# Revit family: 0053938
name_source: partatom
category: Lighting Fixtures
revit_build: Autodesk Revit 2017 (Build: 20190507_1515(x64)
units: mm (PartAtom-declared; Revit-internal decimal feet)

## family parameters
Cut with Voids When Loaded = No
Host = Face
Light Source = Yes
OmniClass Number = 23.80.70.00
OmniClass Title = Lighting
Part Type = Normal
Room Calculation Point = No
Round Connector Dimension = Use Diameter
Shared = No

## types (17) — shared parameters
Assembly Code = D5020200
AssetType = Fixed
CHAMF_2_SYL = 1 mm  [stored 0.00328084 ft]
CHAMF_SYL = 1 mm  [stored 0.00328084 ft]
CLIP_CUTOUT_SYL = 19 mm  [stored 0.062336 ft]
CLIP_HOLE_HE_SYL = 9 mm
CLIP_HOLE_SYL = 3 mm  [stored 0.00984252 ft]
CLIP_SYL = 10 mm  [stored 0.0328084 ft]
ClassificationName = Uniclass2015
ClassificationValue = EF_70_80
Color Filter = 16777215
Default Elevation = 1219 mm
Dimming Lamp Color Temperature Shift = <None>
DocumentationLiterature = http://www.sylvania-lighting.com
ElectricShockClassification = Class II
Emit Shape Visible in Rendering = No
Emit from Circle Diameter = 610 mm
IfcExportAs = IfcLightFixtureType
IfcExportType = IfcLightFixtureType
ImpactProtectionIndex = IK06
IngressProtection = IP44/20
Keynote = 16500
LUM_HEIGHT_SYL = 14 mm  [stored 0.0459318 ft]
Lamp = LED
LampColourRenderingIndex = 80
LampsType = LED
Manufacturer = Feilo Sylvania
ManufacturerName = Feilo Sylvania
Material_1_SYL = <By Category>
Material_2_SYL = <By Category>
Material_3_SYL = <By Category>
Material_4_SYL = <By Category>
Tilt Angle = -90.00°
Type Image = <None>
URL = http://www.sylvania-lighting.com
Voltage = 0 V
zero-valued in all types: Cost

## per-type parameters (varying)
- 0053988 SYLFLAT 105 IP44 550LM 830 DIM: Apparent Load=7 VA; CLIP_DIST_SYL=75 mm  [stored 0.246063 ft]; CLIP_D_SYL=75 mm  [stored 0.246063 ft]; Description=Sylflat DIM is an integrated LED recessed downlight with separated phase dimmable driver; 7W; 550Lm; 79Lm/W; 3000K; IP44 rated from the front; 50,000hrs (L70B50).; LampColourTemperature=3000 K; LampMacAdamStep=3; LampNominalLuminous=550 lm; LuminousEfficacy=78.57 lm/W; Model=Sylflat 105 IP44 550lm 830 DIM; ModelNumber=53988; ModelReference=Sylflat 105 IP44 550lm 830 DIM; Name=Sylflat 105 IP44 550lm 830 DIM; NominalDepth=0 mm  [stored 0 ft]; NominalHeight=0 mm  [stored 0 ft]; NominalLength=0 mm  [stored 0 ft]; Photometric Web File=0053988.ies; PowerConsumption=7 W; PowerFactor=0; R1_SYL=86 mm  [stored 0.282152 ft]; R2_SYL=78 mm; R_DIFF_SYL=64 mm; SIZE_155_SYL=1; SIZE_203_SYL=0; TypeName=Sylflat 105 IP44 550lm 830 DIM; Weight=3.555 kg
- 0053957 SYLFLAT 205 IP44 2250LM 840 DIM: Apparent Load=24 VA; CLIP_DIST_SYL=99 mm  [stored 0.324803 ft]; CLIP_D_SYL=99 mm  [stored 0.324803 ft]; Description=Sylflat DIM is an integrated LED recessed downlight with separated phase dimmable driver; 24W; 2250Lm; 103Lm/W; 4000K; IP44 rated from the front; 50,000hrs (L70B50).; LampColourTemperature=4000 K; LampMacAdamStep=3; LampNominalLuminous=2250 lm; LuminousEfficacy=103 lm/W; Model=Sylflat 205 IP44 2250lm 840 DIM; ModelNumber=53957; ModelReference=Sylflat 205 IP44 2250lm 840 DIM; Name=Sylflat 205 IP44 2250lm 840 DIM; NominalDepth=226 mm  [stored 0.74147 ft]; NominalHeight=21 mm  [stored 0.0688976 ft]; NominalLength=226 mm  [stored 0.74147 ft]; Photometric Web File=0053957.ies; PowerConsumption=24 W; PowerFactor=0.9; R1_SYL=113 mm  [stored 0.370735 ft]; R2_SYL=102 mm; R_DIFF_SYL=87 mm; SIZE_155_SYL=0; SIZE_203_SYL=1; TypeName=Sylflat 205 IP44 2250lm 840 DIM; Weight=4.57 kg
- 0053956 SYLFLAT 205 IP44 2200LM 830 DIM: Apparent Load=24 VA; CLIP_DIST_SYL=99 mm  [stored 0.324803 ft]; CLIP_D_SYL=99 mm  [stored 0.324803 ft]; Description=Sylflat DIM is an integrated LED recessed downlight with separated phase dimmable driver; 24W; 2200Lm; 100Lm/W; 3000K; IP44 rated from the front; 50,000hrs (L70B50).; LampColourTemperature=3000 K; LampMacAdamStep=3; LampNominalLuminous=2200 lm; LuminousEfficacy=100 lm/W; Model=Sylflat 205 IP44 2200lm 830 DIM; ModelNumber=53956; ModelReference=Sylflat 205 IP44 2200lm 830 DIM; Name=Sylflat 205 IP44 2200lm 830 DIM; NominalDepth=226 mm  [stored 0.74147 ft]; NominalHeight=21 mm  [stored 0.0688976 ft]; NominalLength=226 mm  [stored 0.74147 ft]; Photometric Web File=0053956.ies; PowerConsumption=24 W; PowerFactor=0.9; R1_SYL=113 mm  [stored 0.370735 ft]; R2_SYL=102 mm; R_DIFF_SYL=87 mm; SIZE_155_SYL=0; SIZE_203_SYL=1; TypeName=Sylflat 205 IP44 2200lm 830 DIM; Weight=4.57 kg
- 0053955 SYLFLAT 205 IP44 1750LM 840 DIM: Apparent Load=17 VA; CLIP_DIST_SYL=99 mm  [stored 0.324803 ft]; CLIP_D_SYL=99 mm  [stored 0.324803 ft]; Description=Sylflat DIM is an integrated LED recessed downlight with separated phase dimmable driver; 17W; 1750Lm; 103Lm/W; 4000K; IP44 rated from the front; 50,000hrs (L70B50).; LampColourTemperature=4000 K; LampMacAdamStep=3; LampNominalLuminous=1750 lm; LuminousEfficacy=103 lm/W; Material=aluminium housing, other diffuser; Model=Sylflat 205 IP44 1750lm 840 DIM; ModelNumber=53955; ModelReference=Sylflat 205 IP44 1750lm 840 DIM; Name=Sylflat 205 IP44 1750lm 840 DIM; NominalDepth=226 mm  [stored 0.74147 ft]; NominalHeight=21 mm  [stored 0.0688976 ft]; NominalLength=226 mm  [stored 0.74147 ft]; Photometric Web File=0053955.ies; PowerConsumption=17 W; PowerFactor=0.9; R1_SYL=113 mm  [stored 0.370735 ft]; R2_SYL=102 mm; R_DIFF_SYL=87 mm; SIZE_155_SYL=0; SIZE_203_SYL=1; TypeName=Sylflat 205 IP44 1750lm 840 DIM; Weight=4.57 kg
- 0053954 SYLFLAT 205 IP44 1550LM 830 DIM: Apparent Load=17 VA; CLIP_DIST_SYL=99 mm  [stored 0.324803 ft]; CLIP_D_SYL=99 mm  [stored 0.324803 ft]; Description=Sylflat DIM is an integrated LED recessed downlight with separated phase dimmable driver; 17W; 1550Lm; 91Lm/W; 3000K; IP44 rated from the front; 50,000hrs (L70B50).; LampColourTemperature=3000 K; LampMacAdamStep=3; LampNominalLuminous=1550 lm; LuminousEfficacy=91 lm/W; Material=aluminium housing, other diffuser; Model=Sylflat 205 IP44 1550lm 830 DIM; ModelNumber=53954; ModelReference=Sylflat 205 IP44 1550lm 830 DIM; Name=Sylflat 205 IP44 1550lm 830 DIM; NominalDepth=226 mm  [stored 0.74147 ft]; NominalHeight=21 mm  [stored 0.0688976 ft]; NominalLength=226 mm  [stored 0.74147 ft]; Photometric Web File=0053954.ies; PowerConsumption=17 W; PowerFactor=0.9; R1_SYL=113 mm  [stored 0.370735 ft]; R2_SYL=102 mm; R_DIFF_SYL=87 mm; SIZE_155_SYL=0; SIZE_203_SYL=1; TypeName=Sylflat 205 IP44 1550lm 830 DIM; Weight=4.57 kg
- 0053953 SYLFLAT 155 IP44 1100LM 840 DIM: Apparent Load=12 VA; CLIP_DIST_SYL=75 mm  [stored 0.246063 ft]; CLIP_D_SYL=75 mm  [stored 0.246063 ft]; Description=Sylflat DIM is an integrated LED recessed downlight with separated phase dimmable driver; 12W; 1100Lm; 92Lm/W; 4000K; IP44 rated from the front; 50,000hrs (L70B50).; LampColourTemperature=4000 K; LampMacAdamStep=3; LampNominalLuminous=1100 lm; LuminousEfficacy=92 lm/W; Material=aluminium housing, other diffuser; Model=Sylflat 155 IP44 1100lm 840 DIM; ModelNumber=53953; ModelReference=Sylflat 155 IP44 1100lm 840 DIM; Name=Sylflat 155 IP44 1100lm 840 DIM; NominalDepth=172 mm  [stored 0.564304 ft]; NominalHeight=21 mm  [stored 0.0688976 ft]; NominalLength=172 mm  [stored 0.564304 ft]; Photometric Web File=0053953.ies; PowerConsumption=12 W; PowerFactor=0.9; R1_SYL=86 mm  [stored 0.282152 ft]; R2_SYL=78 mm; R_DIFF_SYL=64 mm; SIZE_155_SYL=1; SIZE_203_SYL=0; TypeName=Sylflat 155 IP44 1100lm 840 DIM; Weight=3.27 kg
- 0053952 SYLFLAT 155 IP44 1000LM 830 DIM: Apparent Load=12 VA; CLIP_DIST_SYL=75 mm  [stored 0.246063 ft]; CLIP_D_SYL=75 mm  [stored 0.246063 ft]; Description=Sylflat DIM is an integrated LED recessed downlight with separated phase dimmable driver; 12W; 1000Lm; 83Lm/W; 3000K; IP44 rated from the front; 50,000hrs (L70B50).; LampColourTemperature=3000 K; LampMacAdamStep=3; LampNominalLuminous=1000 lm; LuminousEfficacy=83 lm/W; Material=aluminium housing, other diffuser; Model=Sylflat 155 IP44 1000lm 830 DIM; ModelNumber=53952; ModelReference=Sylflat 155 IP44 1000lm 830 DIM; Name=Sylflat 155 IP44 1000lm 830 DIM; NominalDepth=172 mm  [stored 0.564304 ft]; NominalHeight=21 mm  [stored 0.0688976 ft]; NominalLength=172 mm  [stored 0.564304 ft]; Photometric Web File=0053952.ies; PowerConsumption=12 W; PowerFactor=0.9; R1_SYL=86 mm  [stored 0.282152 ft]; R2_SYL=78 mm; R_DIFF_SYL=64 mm; SIZE_155_SYL=1; SIZE_203_SYL=0; TypeName=Sylflat 155 IP44 1000lm 830 DIM; Weight=3.27 kg
- 0053951 ST E DOWNLIGHT FLT 205 IP44 2200 865 DIM: Apparent Load=24 VA; CLIP_DIST_SYL=99 mm  [stored 0.324803 ft]; CLIP_D_SYL=99 mm  [stored 0.324803 ft]; Description=START eco Downlight Flat IP44 DIM is an integrated LED recessed downlight with separated phase dimmable driver; 24W; 2200Lm; 92Lm/W; 6500K; IP44 rated from the front; 30,000hrs (L70B50).; LampColourTemperature=6500 K; LampMacAdamStep=5; LampNominalLuminous=2200 lm; LuminousEfficacy=92 lm/W; Model=START eco Downlight Flat 205 IP44 2200lm 865 DIM; ModelNumber=53951; ModelReference=START eco Downlight Flat 205 IP44 2200lm 865 DIM; Name=START eco Downlight Flat 205 IP44 2200lm 865 DIM; NominalDepth=226 mm  [stored 0.74147 ft]; NominalHeight=21 mm  [stored 0.0688976 ft]; NominalLength=226 mm  [stored 0.74147 ft]; Photometric Web File=0053951.ies; PowerConsumption=24 W; PowerFactor=0.9; R1_SYL=113 mm  [stored 0.370735 ft]; R2_SYL=102 mm; R_DIFF_SYL=87 mm; SIZE_155_SYL=0; SIZE_203_SYL=1; TypeName=START eco Downlight Flat 205 IP44 2200lm 865 DIM; Weight=4.57 kg
- 0053950 ST E DOWNLIGHT FLT 205 IP44 1700 865 DIM: Apparent Load=17 VA; CLIP_DIST_SYL=99 mm  [stored 0.324803 ft]; CLIP_D_SYL=99 mm  [stored 0.324803 ft]; Description=START eco Downlight Flat IP44 DIM is an integrated LED recessed downlight with separated phase dimmable driver; 17W; 1700Lm; 100Lm/W; 6500K; IP44 rated from the front; 30,000hrs (L70B50).; LampColourTemperature=6500 K; LampMacAdamStep=5; LampNominalLuminous=1700 lm; LuminousEfficacy=100 lm/W; Material=aluminium housing, other diffuser; Model=START eco Downlight Flat 205 IP44 1700lm 865 DIM; ModelNumber=53950; ModelReference=START eco Downlight Flat 205 IP44 1700lm 865 DIM; Name=START eco Downlight Flat 205 IP44 1700lm 865 DIM; NominalDepth=226 mm  [stored 0.74147 ft]; NominalHeight=21 mm  [stored 0.0688976 ft]; NominalLength=226 mm  [stored 0.74147 ft]; Photometric Web File=0053950.ies; PowerConsumption=17 W; PowerFactor=0.9; R1_SYL=113 mm  [stored 0.370735 ft]; R2_SYL=102 mm; R_DIFF_SYL=87 mm; SIZE_155_SYL=0; SIZE_203_SYL=1; TypeName=START eco Downlight Flat 205 IP44 1700lm 865 DIM; Weight=4.57 kg
- 0053949 ST E DOWNLIGHT FLT 155 IP44 1100 865 DIM: Apparent Load=12 VA; CLIP_DIST_SYL=75 mm  [stored 0.246063 ft]; CLIP_D_SYL=75 mm  [stored 0.246063 ft]; Description=START eco Downlight Flat IP44 DIM is an integrated LED recessed downlight with separated phase dimmable driver; 12W; 1100Lm; 92Lm/W; 6500K; IP44 rated from the front; 30,000hrs (L70B50).; LampColourTemperature=6500 K; LampMacAdamStep=5; LampNominalLuminous=1100 lm; LuminousEfficacy=92 lm/W; Material=aluminium housing, other diffuser; Model=START eco Downlight Flat 155 IP44 1100lm 865 DIM; ModelNumber=53949; ModelReference=START eco Downlight Flat 155 IP44 1100lm 865 DIM; Name=START eco Downlight Flat 155 IP44 1100lm 865 DIM; NominalDepth=172 mm  [stored 0.564304 ft]; NominalHeight=21 mm  [stored 0.0688976 ft]; NominalLength=172 mm  [stored 0.564304 ft]; Photometric Web File=0053949.ies; PowerConsumption=12 W; PowerFactor=0.9; R1_SYL=86 mm  [stored 0.282152 ft]; R2_SYL=78 mm; R_DIFF_SYL=64 mm; SIZE_155_SYL=1; SIZE_203_SYL=0; TypeName=START eco Downlight Flat 155 IP44 1100lm 865 DIM; Weight=3.27 kg
- 0053944 ST E DOWNLIGHT FLT 205 IP44 2250 840 DIM: Apparent Load=24 VA; CLIP_DIST_SYL=99 mm  [stored 0.324803 ft]; CLIP_D_SYL=99 mm  [stored 0.324803 ft]; Description=START eco Downlight Flat IP44 DIM is an integrated LED recessed downlight with separated phase dimmable driver; 24W; 2250Lm; 94Lm/W; 4000K; IP44 rated from the front; 30,000hrs (L70B50).; LampColourTemperature=4000 K; LampMacAdamStep=5; LampNominalLuminous=2250 lm; LuminousEfficacy=94 lm/W; Model=START eco Downlight Flat 205 IP44 2250lm 840 DIM; ModelNumber=53944; ModelReference=START eco Downlight Flat 205 IP44 2250lm 840 DIM; Name=START eco Downlight Flat 205 IP44 2250lm 840 DIM; NominalDepth=226 mm  [stored 0.74147 ft]; NominalHeight=21 mm  [stored 0.0688976 ft]; NominalLength=226 mm  [stored 0.74147 ft]; Photometric Web File=0053944.ies; PowerConsumption=24 W; PowerFactor=0.9; R1_SYL=113 mm  [stored 0.370735 ft]; R2_SYL=102 mm; R_DIFF_SYL=87 mm; SIZE_155_SYL=0; SIZE_203_SYL=1; TypeName=START eco Downlight Flat 205 IP44 2250lm 840 DIM; Weight=4.57 kg
- 0053942 ST E DOWNLIGHT FLT 205 IP44 1750 840 DIM: Apparent Load=17 VA; CLIP_DIST_SYL=99 mm  [stored 0.324803 ft]; CLIP_D_SYL=99 mm  [stored 0.324803 ft]; Description=START eco Downlight Flat IP44 DIM is an integrated LED recessed downlight with separated phase dimmable driver; 17W; 1750Lm; 103Lm/W; 4000K; IP44 rated from the front; 30,000hrs (L70B50).; LampColourTemperature=4000 K; LampMacAdamStep=5; LampNominalLuminous=1750 lm; LuminousEfficacy=103 lm/W; Material=aluminium housing, other diffuser; Model=START eco Downlight Flat 205 IP44 1750lm 840 DIM; ModelNumber=53942; ModelReference=START eco Downlight Flat 205 IP44 1750lm 840 DIM; Name=START eco Downlight Flat 205 IP44 1750lm 840 DIM; NominalDepth=226 mm  [stored 0.74147 ft]; NominalHeight=21 mm  [stored 0.0688976 ft]; NominalLength=226 mm  [stored 0.74147 ft]; Photometric Web File=0053942.ies; PowerConsumption=17 W; PowerFactor=0.9; R1_SYL=113 mm  [stored 0.370735 ft]; R2_SYL=102 mm; R_DIFF_SYL=87 mm; SIZE_155_SYL=0; SIZE_203_SYL=1; TypeName=START eco Downlight Flat 205 IP44 1750lm 840 DIM; Weight=4.57 kg
- 0053941 ST E DOWNLIGHT FLT 155 IP44 1100 840 DIM: Apparent Load=12 VA; CLIP_DIST_SYL=75 mm  [stored 0.246063 ft]; CLIP_D_SYL=75 mm  [stored 0.246063 ft]; Description=START eco Downlight Flat IP44 DIM is an integrated LED recessed downlight with separated phase dimmable driver; 12W; 1100Lm; 92Lm/W; 4000K; IP44 rated from the front; 30,000hrs (L70B50).; LampColourTemperature=4000 K; LampMacAdamStep=5; LampNominalLuminous=1100 lm; LuminousEfficacy=92 lm/W; Material=aluminium housing, other diffuser; Model=START eco Downlight Flat 155 IP44 1100lm 840 DIM; ModelNumber=53941; ModelReference=START eco Downlight Flat 155 IP44 1100lm 840 DIM; Name=START eco Downlight Flat 155 IP44 1100lm 840 DIM; NominalDepth=172 mm  [stored 0.564304 ft]; NominalHeight=21 mm  [stored 0.0688976 ft]; NominalLength=172 mm  [stored 0.564304 ft]; Photometric Web File=0053941.ies; PowerConsumption=12 W; PowerFactor=0.9; R1_SYL=86 mm  [stored 0.282152 ft]; R2_SYL=78 mm; R_DIFF_SYL=64 mm; SIZE_155_SYL=1; SIZE_203_SYL=0; TypeName=START eco Downlight Flat 155 IP44 1100lm 840 DIM; Weight=3.27 kg
- 0053940 ST E DOWNLIGHT FLT 205 IP44 2200 830 DIM: Apparent Load=24 VA; CLIP_DIST_SYL=99 mm  [stored 0.324803 ft]; CLIP_D_SYL=99 mm  [stored 0.324803 ft]; Description=START eco Downlight Flat IP44 DIM is an integrated LED recessed downlight with separated phase dimmable driver; 24W; 2200Lm; 92Lm/W; 3000K; IP44 rated from the front; 30,000hrs (L70B50).; LampColourTemperature=3000 K; LampMacAdamStep=5; LampNominalLuminous=2200 lm; LuminousEfficacy=92 lm/W; Model=START eco Downlight Flat 205 IP44 2200lm 830 DIM; ModelNumber=53940; ModelReference=START eco Downlight Flat 205 IP44 2200lm 830 DIM; Name=START eco Downlight Flat 205 IP44 2200lm 830 DIM; NominalDepth=226 mm  [stored 0.74147 ft]; NominalHeight=21 mm  [stored 0.0688976 ft]; NominalLength=226 mm  [stored 0.74147 ft]; Photometric Web File=0053940.ies; PowerConsumption=24 W; PowerFactor=0.9; R1_SYL=113 mm  [stored 0.370735 ft]; R2_SYL=102 mm; R_DIFF_SYL=87 mm; SIZE_155_SYL=0; SIZE_203_SYL=1; TypeName=START eco Downlight Flat 205 IP44 2200lm 830 DIM; Weight=4.57 kg
- 0053938 ST E DOWNLIGHT FLT 205 IP44 1550 830 DIM: Apparent Load=17 VA; CLIP_DIST_SYL=99 mm  [stored 0.324803 ft]; CLIP_D_SYL=99 mm  [stored 0.324803 ft]; Description=START eco Downlight Flat IP44 DIM is an integrated LED recessed downlight with separated phase dimmable driver; 17W; 1550Lm; 91Lm/W; 3000K; IP44 rated from the front; 30,000hrs (L70B50).; LampColourTemperature=3000 K; LampMacAdamStep=5; LampNominalLuminous=1550 lm; LuminousEfficacy=91 lm/W; Material=aluminium housing, other diffuser; Model=START eco Downlight Flat 205 IP44 1550lm 830 DIM; ModelNumber=0053938; ModelReference=START eco Downlight Flat 205 IP44 1550lm 830 DIM; Name=START eco Downlight Flat 205 IP44 1550lm 830 DIM; NominalDepth=226 mm  [stored 0.74147 ft]; NominalHeight=21 mm  [stored 0.0688976 ft]; NominalLength=226 mm  [stored 0.74147 ft]; Photometric Web File=0053938.ies; PowerConsumption=17 W; PowerFactor=0.9; R1_SYL=113 mm  [stored 0.370735 ft]; R2_SYL=102 mm; R_DIFF_SYL=87 mm; SIZE_155_SYL=0; SIZE_203_SYL=1; TypeName=START eco Downlight Flat 205 IP44 1550lm 830 DIM; Weight=4.57 kg
- 0053937 ST E DOWNLIGHT FLT 155 IP44 1000 830 DIM: Apparent Load=12 VA; CLIP_DIST_SYL=75 mm  [stored 0.246063 ft]; CLIP_D_SYL=75 mm  [stored 0.246063 ft]; Description=START eco Downlight Flat IP44 DIM is an integrated LED recessed downlight with separated phase dimmable driver; 12W; 1000Lm; 83Lm/W; 3000K; IP44 rated from the front; 30,000hrs (L70B50).; LampColourTemperature=3000 K; LampMacAdamStep=5; LampNominalLuminous=1000 lm; LuminousEfficacy=83 lm/W; Material=aluminium housing, other diffuser; Model=START eco Downlight Flat 155 IP44 1000lm 830 DIM; ModelNumber=53937; ModelReference=START eco Downlight Flat 155 IP44 1000lm 830 DIM; Name=START eco Downlight Flat 155 IP44 1000lm 830 DIM; NominalDepth=172 mm  [stored 0.564304 ft]; NominalHeight=21 mm  [stored 0.0688976 ft]; NominalLength=172 mm  [stored 0.564304 ft]; Photometric Web File=0053937.ies; PowerConsumption=12 W; PowerFactor=0.9; R1_SYL=86 mm  [stored 0.282152 ft]; R2_SYL=78 mm; R_DIFF_SYL=64 mm; SIZE_155_SYL=1; SIZE_203_SYL=0; TypeName=START eco Downlight Flat 155 IP44 1000lm 830 DIM; Weight=3.27 kg
- 0053989 SYLFLAT 105 IP44 600LM 840 DIM: Apparent Load=7 VA; CLIP_DIST_SYL=75 mm  [stored 0.246063 ft]; CLIP_D_SYL=75 mm  [stored 0.246063 ft]; Description=Sylflat DIM is an integrated LED recessed downlight with separated phase dimmable driver; 7W; 600Lm; 86Lm/W; 4000K; IP44 rated from the front; 50,000hrs (L70B50).; LampColourTemperature=4000 K; LampMacAdamStep=3; LampNominalLuminous=600 lm; LuminousEfficacy=85.71 lm/W; Model=Sylflat 105 IP44 600lm 840 DIM; ModelNumber=53989; ModelReference=Sylflat 105 IP44 600lm 840 DIM; Name=Sylflat 105 IP44 600lm 840 DIM; NominalDepth=0 mm  [stored 0 ft]; NominalHeight=0 mm  [stored 0 ft]; NominalLength=0 mm  [stored 0 ft]; Photometric Web File=0053989.ies; PowerConsumption=7 W; PowerFactor=0; R1_SYL=86 mm  [stored 0.282152 ft]; R2_SYL=78 mm; R_DIFF_SYL=64 mm; SIZE_155_SYL=1; SIZE_203_SYL=0; TypeName=Sylflat 105 IP44 600lm 840 DIM; Weight=3.555 kg

note: [stored X ft] marks values corroborated as IEEE doubles in the binary element streams (Revit-internal decimal feet)

## geometry (parser evidence)
native form markers: Sweep x3
no freeform markers — native parametric forms only
